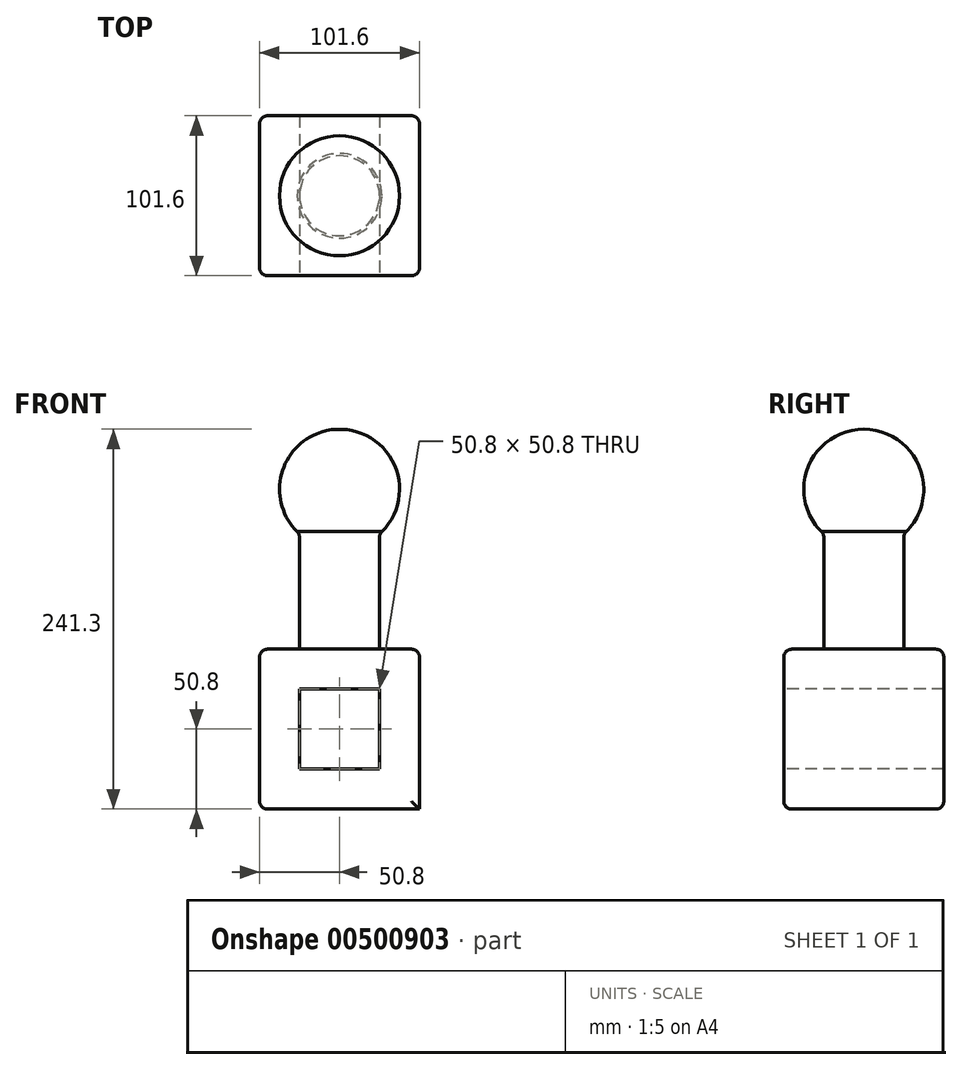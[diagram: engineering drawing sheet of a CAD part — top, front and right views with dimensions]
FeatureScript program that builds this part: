
annotation { "Feature Type Name" : "Feature", "Feature Type Description" : "" }
export const myFeature = defineFeature(function(context is Context, id is Id, definition is map)
    precondition{}
    {
        {
            var Q0;
            Q0=qCreatedBy(makeId("Top.planeOp"),FACE);
            var sketch = newSketch(context, id + "F0", { "sketchPlane" : qUnion([Q0])});
            skLineSegment(sketch, "E0.bottom", {"start": v(50.8, 50.8) * mm, "end": v(-50.8, 50.8) * mm});
            skLineSegment(sketch, "E0.top", {"start": v(50.8, -50.8) * mm, "end": v(-50.8, -50.8) * mm});
            skLineSegment(sketch, "E0.left", {"start": v(50.8, 50.8) * mm, "end": v(50.8, -50.8) * mm});
            skLineSegment(sketch, "E0.right", {"start": v(-50.8, 50.8) * mm, "end": v(-50.8, -50.8) * mm});
            skPoint(sketch, "E0.middle", {"position": v(0, 0) * mm});
            skSolve(sketch);
        }
        {
            var Q0;
            Q0=makeQuery(id+"F0.imprint","IMPRINT",FACE,{"disambiguationData":[TD([[makeQuery(id+"F0.imprint","IMPRINT",EDGE,{"derivedFrom":sQuery(id+"F0.wireOp",EDGE,"E0.bottom")}),1.0]])]});
            extrude(context, id + "F1", {"entities" : qUnion([Q0]), "depth" : 101.6 * mm});
        }
        {
            var Q0;
            Q0=makeQuery(id+"F1.opExtrude","CAP_FACE",FACE,{"disambiguationData":[OSD([sQuery(id+"F0.wireOp",EDGE,"E0.bottom"),sQuery(id+"F0.wireOp",EDGE,"E0.top"),sQuery(id+"F0.wireOp",EDGE,"E0.left"),sQuery(id+"F0.wireOp",EDGE,"E0.right")])],"isStart":false});
            var sketch = newSketch(context, id + "F2", { "sketchPlane" : qUnion([Q0])});
            skCircle(sketch, "E1", {"center": v(0, 0) * mm, "radius": 25.4 * mm});
            skSolve(sketch);
        }
        {
            var Q0;
            Q0=makeQuery(id+"F2.imprint","IMPRINT",FACE,{"disambiguationData":[TD([[makeQuery(id+"F2.imprint","IMPRINT",EDGE,{"derivedFrom":sQuery(id+"F2.wireOp",EDGE,"E1")}),1.0]])]});
            extrude(context, id + "F3", {"entities" : qUnion([Q0]), "operationType" : NewBodyOperationType.ADD, "depth" : 101.6 * mm});
        }
        {
            var Q0;
            Q0=makeQuery(id+"F3.opExtrude","CAP_FACE",FACE,{"disambiguationData":[OSD([sQuery(id+"F2.wireOp",EDGE,"E1")])],"isStart":false});
            var sketch = newSketch(context, id + "F4", { "sketchPlane" : qUnion([Q0])});
            skArc(sketch, "E2", {"start": v(0, -38.1) * mm, "mid": v(38.1, 0) * mm, "end": v(0, 38.1) * mm});
            skLineSegment(sketch, "E3", {"start": v(0, 38.1) * mm, "end": v(0, -38.1) * mm});
            skSolve(sketch);
        }
        {
            var Q0;
            {var subQ0=sQuery(id+"F4.wireOp",EDGE,"E2");Q0=makeQuery(id+"F4.imprint","IMPRINT",FACE,{"disambiguationData":[TD([[makeQuery(id+"F4.imprint","IMPRINT",EDGE,{"derivedFrom":subQ0}),1.0]])]});}
            var Q1;
            {var subQ0=sQuery(id+"F4.wireOp",EDGE,"E3");var subQ1=makeQuery(id+"F3.opExtrude","CAP_EDGE",EDGE,{"disambiguationData":[OSD([sQuery(id+"F2.wireOp",EDGE,"E1")])],"isStart":false});var subQ2=makeQuery(id+"F4.imprint","INTERSECT",VERTEX,{"disambiguationData":[OD(0.0)],"derivedFrom":[subQ1,subQ0]});Q1=makeQuery(id+"F4.imprint","IMPRINT",FACE,{"disambiguationData":[TD([[makeQuery(id+"F4.imprint","IMPRINT",EDGE,{"disambiguationData":[TD([[subQ2,-1.0]])],"derivedFrom":subQ0}),1.0]])]});}
            var Q2;
            Q2=sQuery(id+"F4.wireOp",EDGE,"E3");
            revolve(context, id + "F5", {"operationType" : NewBodyOperationType.ADD, "entities" : qUnion([Q0, Q1]), "axis" : qUnion([Q2]), "revolveType" : RevolveType.FULL});
        }
        {
            var Q0;
            Q0=makeQuery(id+"F1.opExtrude","SWEPT_FACE",FACE,{"disambiguationData":[OSD([sQuery(id+"F0.wireOp",EDGE,"E0.top")])]});
            var sketch = newSketch(context, id + "F6", { "sketchPlane" : qUnion([Q0])});
            skLineSegment(sketch, "E4.bottom", {"start": v(25.4, 76.2) * mm, "end": v(-25.4, 76.2) * mm});
            skLineSegment(sketch, "E4.top", {"start": v(25.4, 25.4) * mm, "end": v(-25.4, 25.4) * mm});
            skLineSegment(sketch, "E4.left", {"start": v(25.4, 76.2) * mm, "end": v(25.4, 25.4) * mm});
            skLineSegment(sketch, "E4.right", {"start": v(-25.4, 76.2) * mm, "end": v(-25.4, 25.4) * mm});
            skPoint(sketch, "E4.middle", {"position": v(0, 50.8) * mm});
            skSolve(sketch);
        }
        {
            var Q0;
            Q0=makeQuery(id+"F6.imprint","IMPRINT",FACE,{"disambiguationData":[TD([[makeQuery(id+"F6.imprint","IMPRINT",EDGE,{"derivedFrom":sQuery(id+"F6.wireOp",EDGE,"E4.bottom")}),1.0]])]});
            extrude(context, id + "F7", {"entities" : qUnion([Q0]), "operationType" : NewBodyOperationType.REMOVE, "oppositeDirection" : true, "depth" : 101.6 * mm});
        }
        {
            var Q0;
            Q0=makeQuery(id+"F1.opExtrude","CAP_EDGE",EDGE,{"disambiguationData":[OSD([sQuery(id+"F0.wireOp",EDGE,"E0.left")])],"isStart":false});
            var Q1;
            Q1=makeQuery(id+"F1.opExtrude","CAP_EDGE",EDGE,{"disambiguationData":[OSD([sQuery(id+"F0.wireOp",EDGE,"E0.bottom")])],"isStart":false});
            var Q2;
            Q2=makeQuery(id+"F1.opExtrude","CAP_EDGE",EDGE,{"disambiguationData":[OSD([sQuery(id+"F0.wireOp",EDGE,"E0.top")])],"isStart":false});
            var Q3;
            Q3=makeQuery(id+"F1.opExtrude","CAP_EDGE",EDGE,{"disambiguationData":[OSD([sQuery(id+"F0.wireOp",EDGE,"E0.right")])],"isStart":false});
            var Q4;
            Q4=makeQuery(id+"F1.opExtrude","SWEPT_EDGE",EDGE,{"disambiguationData":[OSD([sQuery(id+"F0.wireOp",EDGE,"E0.top"),sQuery(id+"F0.wireOp",EDGE,"E0.left")])]});
            var Q5;
            Q5=makeQuery(id+"F1.opExtrude","SWEPT_EDGE",EDGE,{"disambiguationData":[OSD([sQuery(id+"F0.wireOp",EDGE,"E0.bottom"),sQuery(id+"F0.wireOp",EDGE,"E0.left")])]});
            var Q6;
            Q6=makeQuery(id+"F1.opExtrude","CAP_EDGE",EDGE,{"disambiguationData":[OSD([sQuery(id+"F0.wireOp",EDGE,"E0.top")])],"isStart":true});
            var Q7;
            Q7=makeQuery(id+"F1.opExtrude","SWEPT_EDGE",EDGE,{"disambiguationData":[OSD([sQuery(id+"F0.wireOp",EDGE,"E0.top"),sQuery(id+"F0.wireOp",EDGE,"E0.right")])]});
            var Q8;
            Q8=makeQuery(id+"F1.opExtrude","CAP_EDGE",EDGE,{"disambiguationData":[OSD([sQuery(id+"F0.wireOp",EDGE,"E0.right")])],"isStart":true});
            var Q9;
            Q9=makeQuery(id+"F1.opExtrude","CAP_EDGE",EDGE,{"disambiguationData":[OSD([sQuery(id+"F0.wireOp",EDGE,"E0.bottom")])],"isStart":true});
            var Q10;
            Q10=makeQuery(id+"F1.opExtrude","SWEPT_EDGE",EDGE,{"disambiguationData":[OSD([sQuery(id+"F0.wireOp",EDGE,"E0.bottom"),sQuery(id+"F0.wireOp",EDGE,"E0.right")])]});
            var Q11;
            Q11=makeQuery(id+"F3.opExtrude","CAP_EDGE",EDGE,{"disambiguationData":[OSD([sQuery(id+"F2.wireOp",EDGE,"E1")])],"isStart":true});
            var Q12;
            Q12=makeQuery(id+"F5.boolean.opBoolean","INTERSECT",EDGE,{"derivedFrom":[makeQuery(id+"F3.opExtrude","SWEPT_FACE",FACE,{"disambiguationData":[OSD([sQuery(id+"F2.wireOp",EDGE,"E1")])]}),makeQuery(id+"F5.opRevolve","SWEPT_FACE",FACE,{"disambiguationData":[OSD([sQuery(id+"F4.wireOp",EDGE,"E2")])]})]});
            fillet(context, id + "F8", {"entities" : qUnion([Q0, Q1, Q2, Q3, Q4, Q5, Q6, Q7, Q8, Q9, Q10, Q11, Q12]), "radius" : 5.08 * mm, "tangentPropagation" : true, "allowEdgeOverflow" : false});
        }
    });
